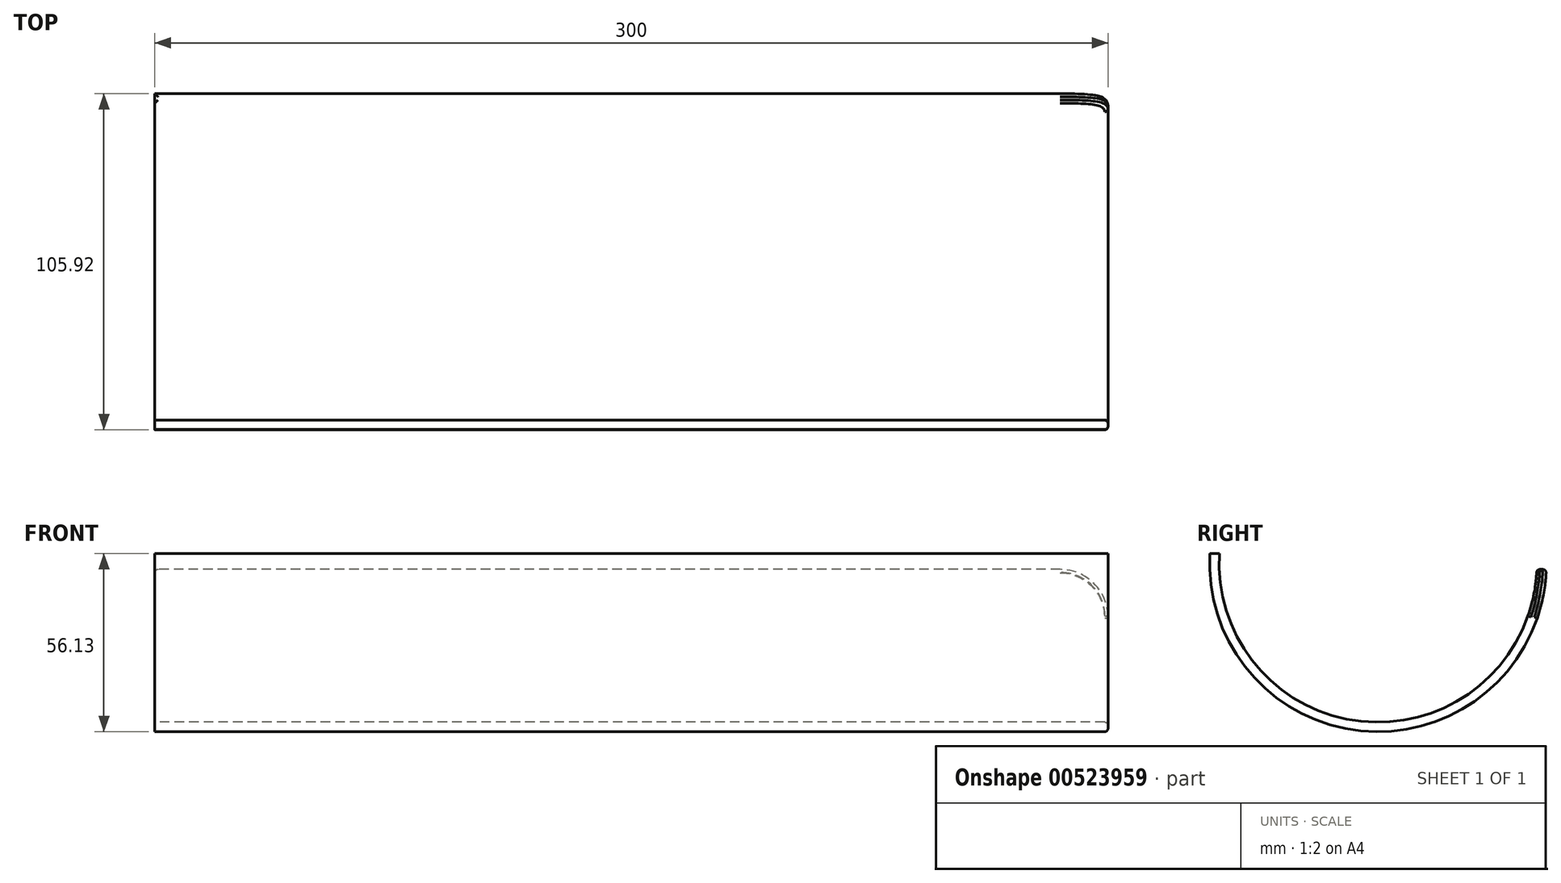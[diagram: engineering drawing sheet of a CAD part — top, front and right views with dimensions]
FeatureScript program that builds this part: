
annotation { "Feature Type Name" : "Feature", "Feature Type Description" : "" }
export const myFeature = defineFeature(function(context is Context, id is Id, definition is map)
    precondition{}
    {
        {
            var Q0;
            Q0=qCreatedBy(makeId("Right.planeOp"),FACE);
            var sketch = newSketch(context, id + "F0", { "sketchPlane" : qUnion([Q0])});
            skCircle(sketch, "E0", {"center": v(0, 1.87) * mm, "radius": 50 * mm});
            skCircle(sketch, "E1.0", {"center": v(0, 1.87) * mm, "radius": 53 * mm});
            skSolve(sketch);
        }
        {
            var Q0;
            Q0=makeQuery(id+"F0.imprint","IMPRINT",FACE,{"disambiguationData":[TD([[makeQuery(id+"F0.imprint","IMPRINT",EDGE,{"derivedFrom":sQuery(id+"F0.wireOp",EDGE,"E0")}),-1.0]])]});
            extrude(context, id + "F1", {"entities" : qUnion([Q0]), "depth" : 300 * mm, "offsetDistance" : 25 * mm});
        }
        {
            var Q0;
            Q0=qCreatedBy(makeId("Right.planeOp"),FACE);
            var sketch = newSketch(context, id + "F2", { "sketchPlane" : qUnion([Q0])});
            skLineSegment(sketch, "E2.bottom", {"start": v(0, 0) * mm, "end": v(-45, 0) * mm});
            skLineSegment(sketch, "E2.top", {"start": v(0, 138.12) * mm, "end": v(-236.33, 138.12) * mm});
            skLineSegment(sketch, "E2.right", {"start": v(-236.33, 0) * mm, "end": v(-236.33, 138.12) * mm});
            skLineSegment(sketch, "E3.bottom", {"start": v(0, 0) * mm, "end": v(150.29, 0) * mm});
            skLineSegment(sketch, "E3.top", {"start": v(0, 138.12) * mm, "end": v(150.29, 138.12) * mm});
            skLineSegment(sketch, "E3.right", {"start": v(150.29, 0) * mm, "end": v(150.29, 138.12) * mm});
            skLineSegment(sketch, "E4.top", {"start": v(-45, 5) * mm, "end": v(-65, 5) * mm});
            skLineSegment(sketch, "E4.left", {"start": v(-45, 0) * mm, "end": v(-45, 5) * mm});
            skLineSegment(sketch, "E4.right", {"start": v(-65, 0) * mm, "end": v(-65, 5) * mm});
            skLineSegment(sketch, "E5.trimOffspring", {"start": v(-65, 0) * mm, "end": v(-236.33, 0) * mm});
            skSolve(sketch);
        }
        {
            var Q0;
            Q0 = qSketchRegion(id + "F2", true);
            extrude(context, id + "F3", {"entities" : qUnion([Q0]), "operationType" : NewBodyOperationType.REMOVE, "endBound" : BoundingType.THROUGH_ALL, "depth" : 25 * mm, "offsetDistance" : 25 * mm});
        }
        {
            var Q0;
            Q0=makeQuery(id+"F3.boolean.opBoolean","INTERSECT",EDGE,{"disambiguationData":[OD(1.0)],"derivedFrom":[makeQuery(id+"F1.opExtrude","CAP_FACE",FACE,{"disambiguationData":[OSD([sQuery(id+"F0.wireOp",EDGE,"E0"),sQuery(id+"F0.wireOp",EDGE,"E1.0")])],"isStart":false}),makeQuery(id+"F3.opExtrude","SWEPT_FACE",FACE,{"disambiguationData":[OSD([sQuery(id+"F2.wireOp",EDGE,"E2.bottom"),sQuery(id+"F2.wireOp",EDGE,"E3.bottom")])]})]});
            var Q1;
            Q1=makeQuery(id+"F3.boolean.opBoolean","INTERSECT",EDGE,{"disambiguationData":[OD(0.0)],"derivedFrom":[makeQuery(id+"F1.opExtrude","CAP_FACE",FACE,{"disambiguationData":[OSD([sQuery(id+"F0.wireOp",EDGE,"E0"),sQuery(id+"F0.wireOp",EDGE,"E1.0")])],"isStart":false}),makeQuery(id+"F3.opExtrude","SWEPT_FACE",FACE,{"disambiguationData":[OSD([sQuery(id+"F2.wireOp",EDGE,"E2.bottom"),sQuery(id+"F2.wireOp",EDGE,"E3.bottom")])]})]});
            var Q2;
            Q2=makeQuery(id+"F3.boolean.opBoolean","COPY",EDGE,{"disambiguationData":[OD(1.0)],"derivedFrom":makeQuery(id+"F3.opExtrude","CAP_EDGE",EDGE,{"disambiguationData":[OSD([sQuery(id+"F2.wireOp",EDGE,"E2.bottom"),sQuery(id+"F2.wireOp",EDGE,"E3.bottom")])],"isStart":true})});
            var Q3;
            Q3=makeQuery(id+"F3.boolean.opBoolean","COPY",EDGE,{"disambiguationData":[OD(0.0)],"derivedFrom":makeQuery(id+"F3.opExtrude","CAP_EDGE",EDGE,{"disambiguationData":[OSD([sQuery(id+"F2.wireOp",EDGE,"E2.bottom"),sQuery(id+"F2.wireOp",EDGE,"E3.bottom")])],"isStart":true})});
            fillet(context, id + "F4", {"entities" : qUnion([Q0, Q1, Q2, Q3]), "radius" : 15 * mm, "tangentPropagation" : true, "allowEdgeOverflow" : false});
        }
        {
            var Q0;
            Q0=makeQuery(id+"F3.boolean.opBoolean","COPY",FACE,{"disambiguationData":[OD(1.0)],"derivedFrom":makeQuery(id+"F3.opExtrude","SWEPT_FACE",FACE,{"disambiguationData":[OSD([sQuery(id+"F2.wireOp",EDGE,"E2.bottom"),sQuery(id+"F2.wireOp",EDGE,"E3.bottom")])]})});
            var Q1;
            Q1=makeQuery(id+"F3.boolean.opBoolean","COPY",FACE,{"disambiguationData":[OD(0.0)],"derivedFrom":makeQuery(id+"F3.opExtrude","SWEPT_FACE",FACE,{"disambiguationData":[OSD([sQuery(id+"F2.wireOp",EDGE,"E2.bottom"),sQuery(id+"F2.wireOp",EDGE,"E3.bottom")])]})});
            fillet(context, id + "F5", {"entities" : qUnion([Q0, Q1]), "radius" : 1 * mm, "tangentPropagation" : true, "allowEdgeOverflow" : false});
        }
    });
